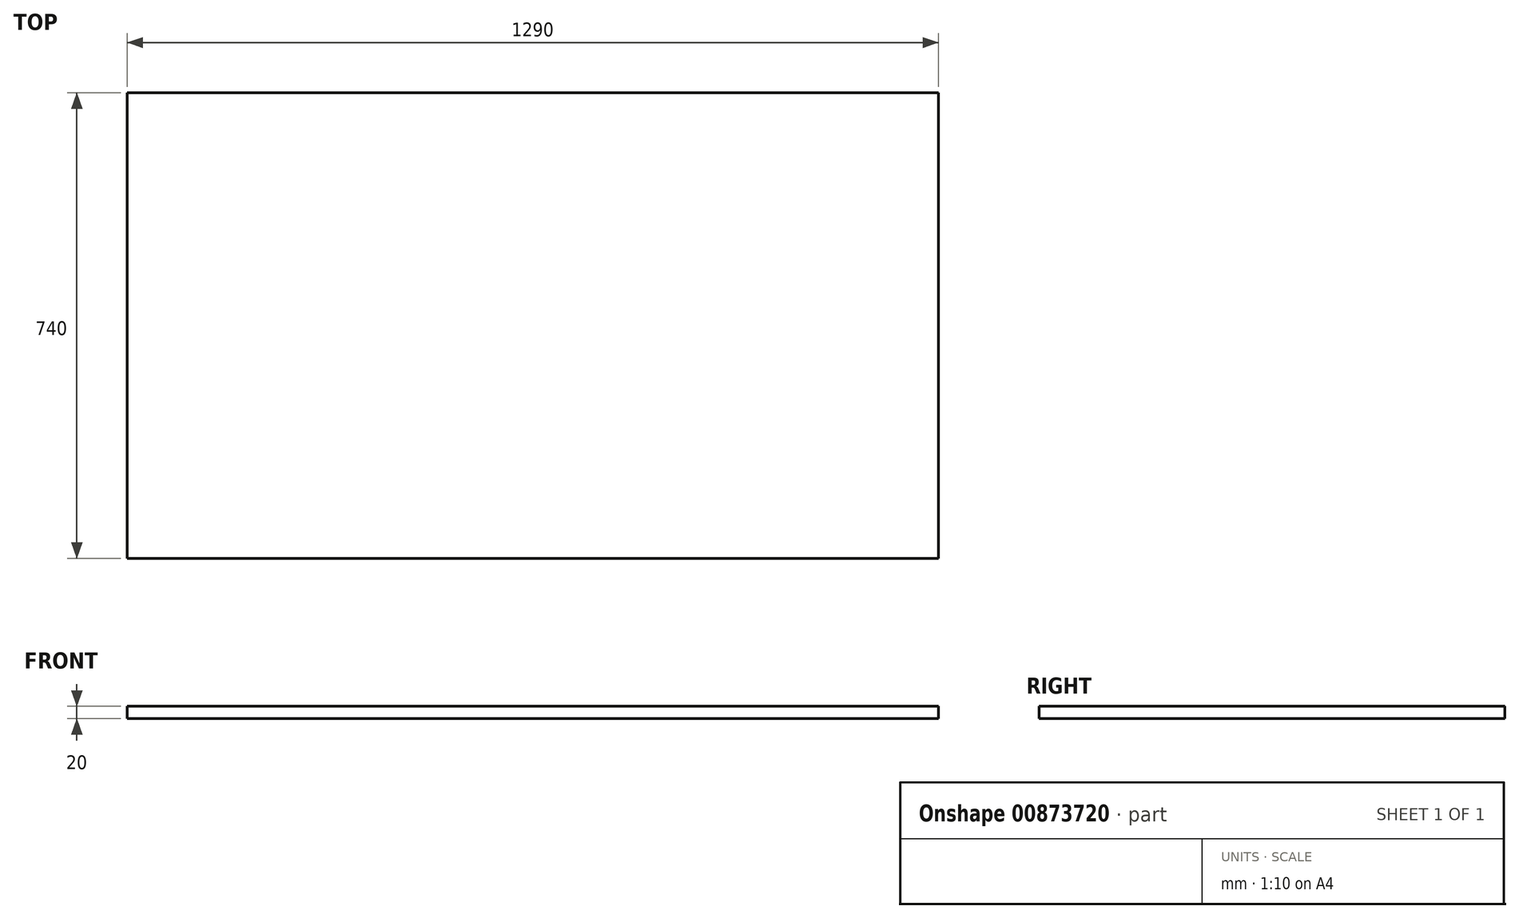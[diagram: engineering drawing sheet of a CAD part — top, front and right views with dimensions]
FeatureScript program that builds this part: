
annotation { "Feature Type Name" : "Feature", "Feature Type Description" : "" }
export const myFeature = defineFeature(function(context is Context, id is Id, definition is map)
    precondition{}
    {
        {
            var Q0;
            Q0=qCreatedBy(makeId("Top.planeOp"),FACE);
            var sketch = newSketch(context, id + "F0", { "sketchPlane" : qUnion([Q0])});
            skLineSegment(sketch, "E0.bottom", {"start": v(0, 0) * mm, "end": v(1290, 0) * mm});
            skLineSegment(sketch, "E0.top", {"start": v(0, 740) * mm, "end": v(1290, 740) * mm});
            skLineSegment(sketch, "E0.left", {"start": v(0, 0) * mm, "end": v(0, 740) * mm});
            skLineSegment(sketch, "E0.right", {"start": v(1290, 0) * mm, "end": v(1290, 740) * mm});
            skSolve(sketch);
        }
        {
            var Q0;
            Q0 = qSketchRegion(id + "F0", true);
            extrude(context, id + "F1", {"entities" : qUnion([Q0]), "depth" : 20 * mm, "offsetDistance" : 25 * mm});
        }
    });
